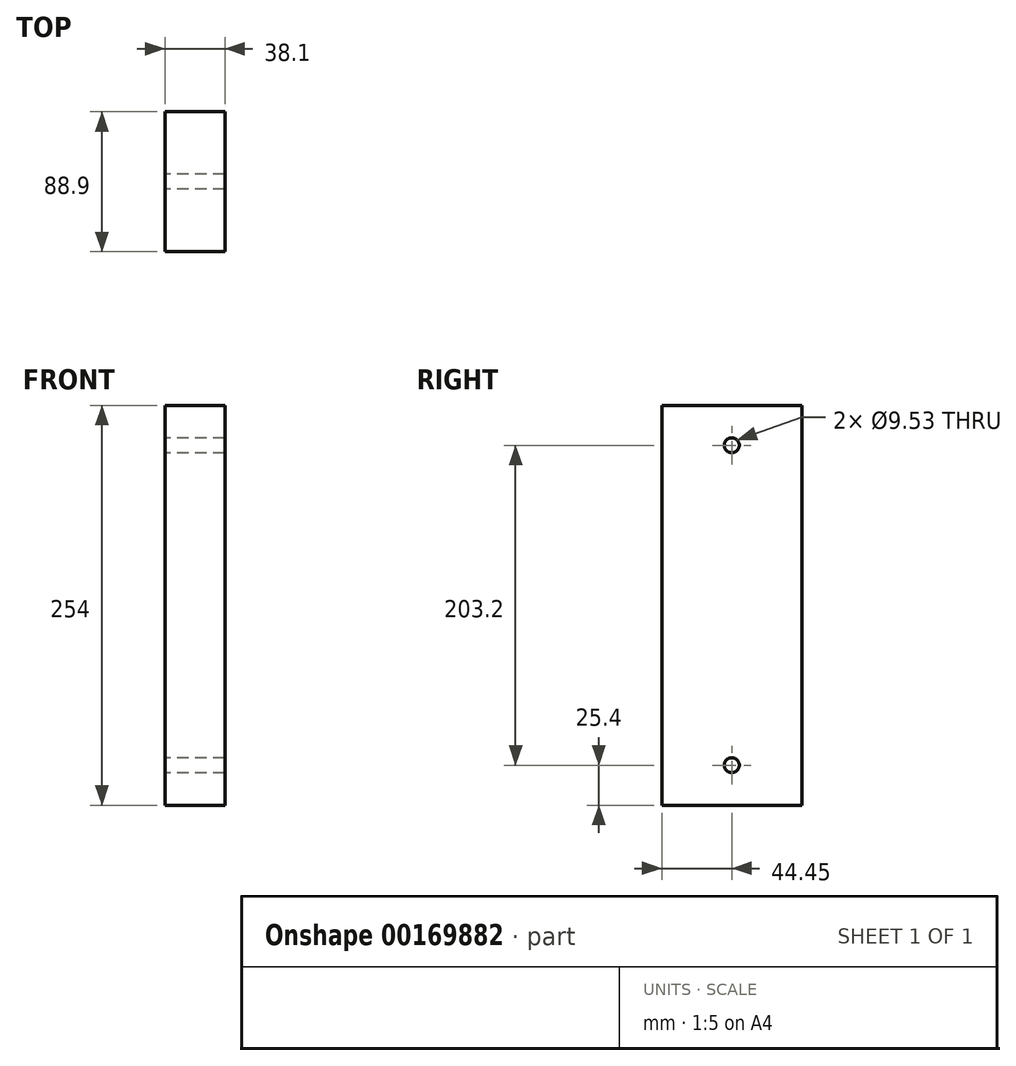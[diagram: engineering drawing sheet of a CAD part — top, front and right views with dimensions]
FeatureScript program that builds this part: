
annotation { "Feature Type Name" : "Feature", "Feature Type Description" : "" }
export const myFeature = defineFeature(function(context is Context, id is Id, definition is map)
    precondition{}
    {
        {
            var Q0;
            Q0=qCreatedBy(makeId("Right.planeOp"),FACE);
            var sketch = newSketch(context, id + "F0", { "sketchPlane" : qUnion([Q0])});
            skLineSegment(sketch, "E0.bottom", {"start": v(-44.45, 127) * mm, "end": v(44.45, 127) * mm});
            skLineSegment(sketch, "E0.top", {"start": v(-44.45, -127) * mm, "end": v(44.45, -127) * mm});
            skLineSegment(sketch, "E0.left", {"start": v(-44.45, 127) * mm, "end": v(-44.45, -127) * mm});
            skLineSegment(sketch, "E0.right", {"start": v(44.45, 127) * mm, "end": v(44.45, -127) * mm});
            skPoint(sketch, "E0.middle", {"position": v(0, 0) * mm});
            skLineSegment(sketch, "E1", {"start": v(0, 127) * mm, "end": v(0, 101.6) * mm, "construction": true});
            skPoint(sketch, "E1.endSnap0", {"position": v(0, 127) * mm});
            skLineSegment(sketch, "E2", {"start": v(0, 101.6) * mm, "end": v(-44.45, 101.6) * mm, "construction": true});
            skLineSegment(sketch, "E3", {"start": v(-44.45, 0) * mm, "end": v(0, 0) * mm, "construction": true});
            skCircle(sketch, "E4", {"center": v(0, 101.6) * mm, "radius": 4.76 * mm});
            skCircle(sketch, "E5.MirrorC", {"center": v(0, -101.6) * mm, "radius": 4.76 * mm});
            skSolve(sketch);
        }
        {
            var Q0;
            Q0 = qSketchRegion(id + "F0", true);
            extrude(context, id + "F1", {"entities" : qUnion([Q0]), "depth" : 38.1 * mm});
        }
    });
